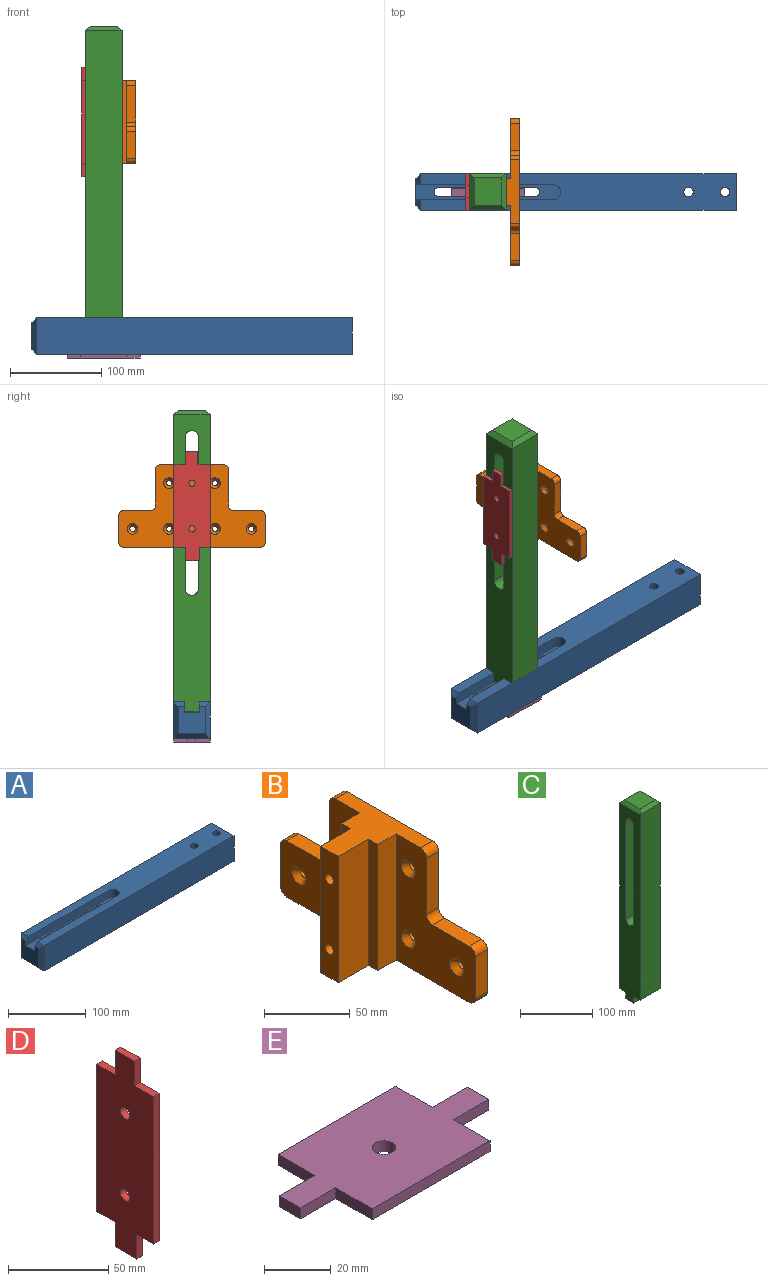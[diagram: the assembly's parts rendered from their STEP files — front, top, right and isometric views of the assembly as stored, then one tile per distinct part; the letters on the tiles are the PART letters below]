
ASSEMBLY  parts=5 mates=10
PART A: 25 faces, bbox 350x40x40 mm
  f0: plane 345x40mm, normal (0,0,1), area 11197.1mm2, adj f2,f3,f4,f6,f7,f12,f13,f14
  f1: plane 30x30mm, normal (-1,0,0), area 787.3mm2, adj f12,f14,f15,f20,f21,f22,f23,f24
  f2: cylinder r=5.15mm len=28mm, axis (0,0,1), area 906mm2, adj f0,f10
  f3: cylinder r=5.15mm len=28mm, axis (0,0,1), area 906mm2, adj f0,f8
  f4: plane 40x40mm, normal (1,0,0), area 1600mm2, adj f0,f5,f6,f7
  f5: plane 345x40mm, normal (0,0,-1), area 12181.2mm2, adj f4,f6,f7,f9,f11,f16,f17,f18
  f6: plane 345x40mm, normal (0,-1,0), area 13800mm2, adj f0,f4,f5,f21
  f7: plane 345x40mm, normal (0,1,0), area 13800mm2, adj f0,f4,f5,f23
  f8: plane 17x17mm, normal (0,0,-1), area 143.7mm2, adj f3,f9
  f9: cylinder r=8.5mm len=17mm, axis (0,0,-1), area 640.9mm2, adj f5,f8
  f10: plane 17x17mm, normal (0,0,-1), area 143.7mm2, adj f2,f11
  f11: cylinder r=8.5mm len=17mm, axis (0,0,-1), area 640.9mm2, adj f5,f10
  f12: plane 150x12mm, normal (0,1,0), area 1787.5mm2, adj f0,f1,f13,f15,f20
  f13: cylinder r=8.05mm len=16.1mm, axis (0,0,1), area 303.5mm2, adj f0,f12,f14,f15
  f14: plane 150x12mm, normal (0,-1,0), area 1787.5mm2, adj f0,f1,f13,f15,f24
  f15: plane 158.05x16.1mm, normal (0,0,1), area 1352mm2, adj f1,f12,f13,f14,f16,f17,f18,f19
  f16: cylinder r=5.15mm len=28mm, axis (0,0,1), area 453mm2, adj f5,f15,f17,f19
  f17: plane 105x28mm, normal (0,1,0), area 2940mm2, adj f5,f15,f16,f18
  f18: cylinder r=5.15mm len=28mm, axis (0,0,1), area 453mm2, adj f5,f15,f17,f19
  f19: plane 105x28mm, normal (0,-1,0), area 2940mm2, adj f5,f15,f16,f18
  f20: plane 11.9x5mm, normal (-0.71,0,0.71), area 66.5mm2, adj f0,f1,f12,f21
  f21: plane 40x5mm, normal (-0.71,-0.71,0), area 247.5mm2, adj f1,f6,f20,f22
  f22: plane 40x5mm, normal (-0.71,0,-0.71), area 247.5mm2, adj f1,f5,f21,f23
  f23: plane 40x5mm, normal (-0.71,0.71,0), area 247.5mm2, adj f1,f7,f22,f24
  f24: plane 12x5mm, normal (-0.71,0,0.71), area 67.2mm2, adj f0,f1,f14,f23
PART B: 42 faces, bbox 50x160x90 mm
  f0: plane 150x50mm, normal (0,0,-1), area 2316mm2, adj f1,f2,f3,f4,f13,f14,f26,f27
  f1: plane 90x15mm, normal (0,-1,0), area 1350mm2, adj f0,f4,f6,f29
  f2: plane 90x15mm, normal (0,1,0), area 1350mm2, adj f0,f6,f27,f31
  f3: plane 90x14.7mm, normal (-1,0,0), area 1250.4mm2, adj f0,f6,f28,f30,f32,f34
  f4: plane 90x65.05mm, normal (-1,0,0), area 3515.7mm2, adj f0,f1,f6,f7,f8,f9,f10,f11
  f5: cylinder r=5mm len=10mm, axis (-1,0,0), area 78.5mm2, adj f6,f25,f26,f27
  f6: plane 70x50mm, normal (0,0,1), area 1516mm2, adj f1,f2,f3,f4,f5,f7,f26,f27
  f7: cylinder r=5mm len=10mm, axis (-1,0,0), area 78.5mm2, adj f4,f6,f8,f26
  f8: plane 40x10mm, normal (0,-1,0), area 400mm2, adj f4,f7,f9,f26
  f9: cylinder r=5mm len=10mm, axis (-1,0,0), area 78.5mm2, adj f4,f8,f10,f26
  f10: plane 30x10mm, normal (0,0,1), area 300mm2, adj f4,f9,f11,f26
  f11: cylinder r=5mm len=10mm, axis (-1,0,0), area 78.5mm2, adj f4,f10,f12,f26
  f12: plane 30x10mm, normal (0,-1,0), area 300mm2, adj f4,f11,f13,f26
  f13: cylinder r=5mm len=10mm, axis (-1,0,0), area 78.5mm2, adj f0,f4,f12,f26
  f14: cylinder r=5mm len=10mm, axis (-1,0,0), area 78.5mm2, adj f0,f15,f26,f27
  f15: plane 30x10mm, normal (0,1,0), area 300mm2, adj f14,f16,f26,f27
  f16: cylinder r=5mm len=10mm, axis (-1,0,0), area 78.5mm2, adj f15,f17,f26,f27
  f17: plane 30x10mm, normal (0,0,1), area 300mm2, adj f16,f18,f26,f27
  f18: cylinder r=5mm len=10mm, axis (-1,0,0), area 78.5mm2, adj f17,f25,f26,f27
  f19: cylinder r=2.9mm len=6mm, axis (-1,0,0), area 109.3mm2, adj f26,f40
  f20: cylinder r=2.9mm len=6mm, axis (-1,0,0), area 109.3mm2, adj f26,f38
  f21: cylinder r=2.9mm len=6mm, axis (-1,0,0), area 109.3mm2, adj f26,f41
  f22: cylinder r=2.9mm len=6mm, axis (-1,0,0), area 109.3mm2, adj f26,f37
  f23: cylinder r=2.9mm len=6mm, axis (-1,0,0), area 109.3mm2, adj f26,f39
  f24: cylinder r=2.9mm len=6mm, axis (-1,0,0), area 109.3mm2, adj f26,f36
  f25: plane 40x10mm, normal (0,1,0), area 400mm2, adj f5,f18,f26,f27
  f26: plane 160x90mm, normal (1,0,0), area 10220mm2, adj f0,f5,f6,f7,f8,f9,f10,f11
  f27: plane 90x65.05mm, normal (-1,0,0), area 3515.7mm2, adj f0,f2,f5,f6,f14,f15,f16,f17
  f28: plane 90x25mm, normal (0,-1,0), area 2250mm2, adj f0,f3,f6,f29
  f29: plane 90x7.6mm, normal (-1,0,0), area 684mm2, adj f0,f1,f6,f28
  f30: plane 90x25mm, normal (0,1,0), area 2250mm2, adj f0,f3,f6,f31
  f31: plane 90x7.6mm, normal (-1,0,0), area 684mm2, adj f0,f2,f6,f30
  f32: cylinder r=3.4mm len=30mm, axis (-1,0,0), area 640.9mm2, adj f3,f33
  f33: plane 6.8x6.8mm, normal (-1,0,0), area 36.3mm2, adj f32
  f34: cylinder r=3.4mm len=30mm, axis (-1,0,0), area 640.9mm2, adj f3,f35
  f35: plane 6.8x6.8mm, normal (-1,0,0), area 36.3mm2, adj f34
  f36: cone r=5.9mm half-angle=36.9deg, axis (-1,0,0), area 138.2mm2, adj f24,f27
  f37: cone r=5.9mm half-angle=36.9deg, axis (-1,0,0), area 138.2mm2, adj f22,f27
  f38: cone r=5.9mm half-angle=36.9deg, axis (-1,0,0), area 138.2mm2, adj f4,f20
  f39: cone r=5.9mm half-angle=36.9deg, axis (-1,0,0), area 138.2mm2, adj f4,f23
  f40: cone r=5.9mm half-angle=36.9deg, axis (-1,0,0), area 138.2mm2, adj f4,f19
  f41: cone r=5.9mm half-angle=36.9deg, axis (-1,0,0), area 138.2mm2, adj f21,f27
PART C: 25 faces, bbox 40x40x330 mm
  f0: plane 195.16x30.16mm, normal (1,0,0), area 3012.7mm2, adj f13,f14,f15,f16,f17,f18,f19,f20
  f1: plane 325x40mm, normal (1,0,0), area 7071.6mm2, adj f2,f3,f4,f7,f8,f9,f10,f13
  f2: plane 40x16mm, normal (0,0,-1), area 601.5mm2, adj f1,f6,f7,f9,f11
  f3: plane 314x40mm, normal (0,-1,0), area 12560mm2, adj f1,f6,f10,f24
  f4: plane 314x40mm, normal (0,1,0), area 12560mm2, adj f1,f6,f8,f21
  f5: plane 30x30mm, normal (0,0,1), area 900mm2, adj f21,f22,f23,f24
  f6: plane 325x40mm, normal (-1,0,0), area 10084.3mm2, adj f2,f3,f4,f7,f8,f9,f10,f17
  f7: plane 40x11mm, normal (0,1,0), area 440mm2, adj f1,f2,f6,f8
  f8: plane 40x12mm, normal (0,0,-1), area 480mm2, adj f1,f4,f6,f7
  f9: plane 40x11mm, normal (0,-1,0), area 440mm2, adj f1,f2,f6,f10
  f10: plane 40x12mm, normal (0,0,-1), area 480mm2, adj f1,f3,f6,f9
  f11: cylinder r=3.5mm len=25mm, axis (0,0,-1), area 549.8mm2, adj f2,f12
  f12: plane 7x7mm, normal (0,0,-1), area 38.5mm2, adj f11
  f13: plane 167.19x10mm, normal (0,-1,0), area 1671.9mm2, adj f0,f1,f14,f16
  f14: cylinder r=15.16mm len=30.16mm, axis (1,0,0), area 476.2mm2, adj f0,f1,f13,f15
  f15: plane 162.81x10mm, normal (0,1,0), area 1628.1mm2, adj f0,f1,f14,f16
  f16: cylinder r=15mm len=30mm, axis (1,0,0), area 471.2mm2, adj f0,f1,f13,f15
  f17: cylinder r=7.5mm len=30mm, axis (1,0,0), area 706.9mm2, adj f0,f6,f18,f19
  f18: plane 165x30mm, normal (0,-1,0), area 4950mm2, adj f0,f6,f17,f20
  f19: plane 165x30mm, normal (0,1,0), area 4950mm2, adj f0,f6,f17,f20
  f20: cylinder r=7.5mm len=30mm, axis (1,0,0), area 706.9mm2, adj f0,f6,f18,f19
  f21: plane 40x5mm, normal (0,0.71,0.71), area 247.5mm2, adj f4,f5,f22,f23
  f22: plane 40x5mm, normal (0.71,0,0.71), area 247.5mm2, adj f1,f5,f21,f24
  f23: plane 40x5mm, normal (-0.71,0,0.71), area 247.5mm2, adj f5,f6,f21,f24
  f24: plane 40x5mm, normal (0,-0.71,0.71), area 247.5mm2, adj f3,f5,f22,f23
PART D: 16 faces, bbox 4x40x120 mm
  f0: plane 13.5x4mm, normal (0,0,1), area 54mm2, adj f1,f13,f14,f15
  f1: plane 15x4mm, normal (0,-1,0), area 60mm2, adj f0,f2,f14,f15
  f2: plane 13.5x4mm, normal (0,0,1), area 54mm2, adj f1,f3,f14,f15
  f3: plane 90x4mm, normal (0,-1,0), area 360mm2, adj f2,f4,f14,f15
  f4: plane 11.83x4mm, normal (0,0,-1), area 47.3mm2, adj f3,f5,f14,f15
  f5: plane 15x4mm, normal (0,-1,0), area 60mm2, adj f4,f6,f14,f15
  f6: plane 15.17x4mm, normal (0,0,-1), area 60.7mm2, adj f5,f7,f14,f15
  f7: plane 15x4mm, normal (0,1,0), area 60mm2, adj f6,f8,f14,f15
  f8: plane 13x4mm, normal (0,0,-1), area 52mm2, adj f7,f9,f14,f15
  f9: plane 90x4mm, normal (0,1,0), area 360mm2, adj f8,f10,f14,f15
  f10: plane 13x4mm, normal (0,0,1), area 52mm2, adj f9,f13,f14,f15
  f11: cylinder r=3.4mm len=6.8mm, axis (-1,0,0), area 85.5mm2, adj f14,f15
  f12: cylinder r=3.4mm len=6.8mm, axis (-1,0,0), area 85.5mm2, adj f14,f15
  f13: plane 15x4mm, normal (0,1,0), area 60mm2, adj f0,f10,f14,f15
  f14: plane 120x40mm, normal (1,0,0), area 3957.3mm2, adj f0,f1,f2,f3,f4,f5,f6,f7
  f15: plane 120x40mm, normal (-1,0,0), area 3957.3mm2, adj f0,f1,f2,f3,f4,f5,f6,f7
PART E: 15 faces, bbox 80x40x4 mm
  f0: plane 15.5x4mm, normal (1,0,0), area 62mm2, adj f1,f12,f13,f14
  f1: plane 50x4mm, normal (0,1,0), area 200mm2, adj f0,f2,f13,f14
  f2: plane 15.5x4mm, normal (-1,0,0), area 62mm2, adj f1,f3,f13,f14
  f3: plane 15x4mm, normal (0,1,0), area 60mm2, adj f2,f4,f13,f14
  f4: plane 9x4mm, normal (-1,0,0), area 36mm2, adj f3,f5,f13,f14
  f5: plane 15x4mm, normal (0,-1,0), area 60mm2, adj f4,f6,f13,f14
  f6: plane 15.5x4mm, normal (-1,0,0), area 62mm2, adj f5,f7,f13,f14
  f7: plane 50x4mm, normal (0,-1,0), area 200mm2, adj f6,f8,f13,f14
  f8: plane 15.5x4mm, normal (1,0,0), area 62mm2, adj f7,f9,f13,f14
  f9: plane 15x4mm, normal (0,-1,0), area 60mm2, adj f8,f10,f13,f14
  f10: plane 9x4mm, normal (1,0,0), area 36mm2, adj f9,f12,f13,f14
  f11: cylinder r=3.5mm len=7mm, axis (0,0,-1), area 88mm2, adj f13,f14
  f12: plane 15x4mm, normal (0,1,0), area 60mm2, adj f0,f10,f13,f14
  f13: plane 80x40mm, normal (0,0,1), area 2231.5mm2, adj f0,f1,f2,f3,f4,f5,f6,f7
  f14: plane 80x40mm, normal (0,0,-1), area 2231.5mm2, adj f0,f1,f2,f3,f4,f5,f6,f7
PLACE A t=(-212.63,-32.44,6.4)mm fixed
PLACE B t=(-284.12,-32.69,240.4)mm
PLACE C t=(-309.12,-32.54,180.4)mm fixed
PLACE D rot(axis=(0,1,0),0deg) t=(-333.12,-32.69,240.4)mm
PLACE E rot(axis=(0,0,1),0deg) t=(-309.12,-32.54,-17.6)mm
MATE parallel B.f0 <-> A.f0  axis (0,0,-1) through (-286.7,-32.69,195.4)mm
MATE planar C.f9 <-> A.f12  axis (0,-1,0) through (-309.12,-40.54,20.9)mm
MATE cylindrical D.f12 <-> B.f32  axis (-1,0,0) through (-333.12,-32.69,215.4)mm
MATE cylindrical C.f11 <-> E.f11  axis (0,0,-1) through (-309.12,-32.54,15.4)mm
MATE planar D.f14 <-> C.f6  axis (1,0,0) through (-329.12,-32.71,240.06)mm
MATE cylindrical D.f11 <-> B.f34  axis (-1,0,0) through (-333.12,-32.69,265.4)mm
MATE planar E.f13 <-> A.f5  axis (0,0,1) through (-309.13,-12.54,-13.6)mm
MATE planar C.f0 <-> B.f31  axis (1,0,0) through (-299.12,-17.54,231.8)mm
MATE planar A.f0 <-> C.f10  axis (0,0,1) through (-191.15,-32.43,26.4)mm
MATE planar C.f19 <-> B.f28  axis (0,1,0) through (-314.12,-40.04,232.9)mm
